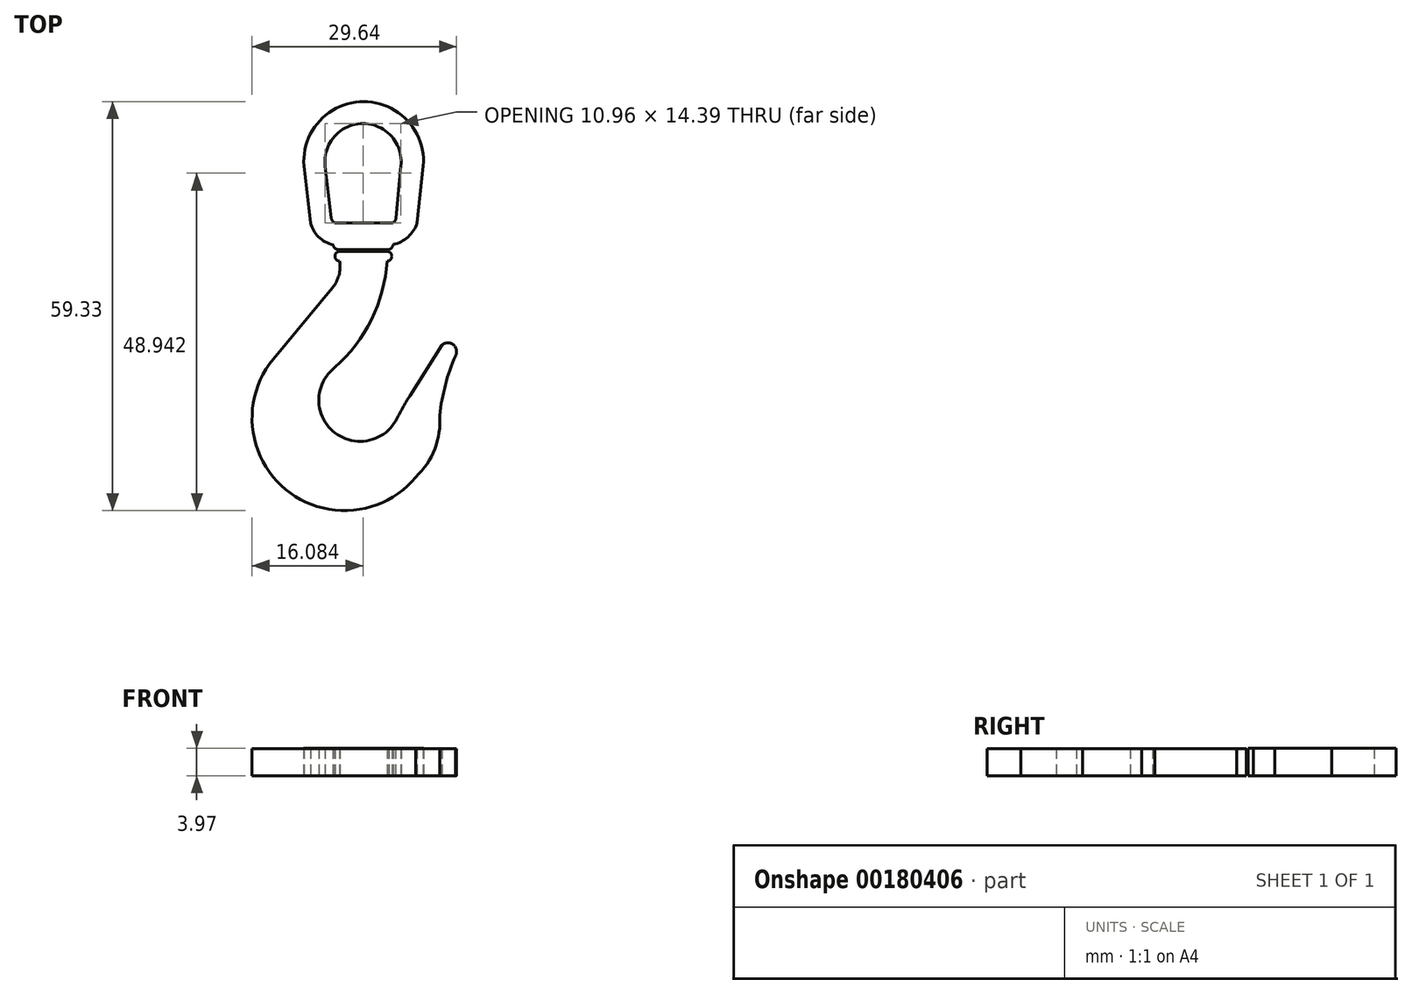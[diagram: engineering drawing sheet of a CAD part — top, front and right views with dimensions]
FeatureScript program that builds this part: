
annotation { "Feature Type Name" : "Feature", "Feature Type Description" : "" }
export const myFeature = defineFeature(function(context is Context, id is Id, definition is map)
    precondition{}
    {
        {
            var Q0;
            Q0=qCreatedBy(makeId("Top.planeOp"),FACE);
            var sketch = newSketch(context, id + "F0", { "sketchPlane" : qUnion([Q0])});
            skLineSegment(sketch, "E0", {"start": v(3.1, -1.85) * mm, "end": v(-3.77, -1.85) * mm});
            skLineSegment(sketch, "E1", {"start": v(-3.77, -3.24) * mm, "end": v(3.1, -3.24) * mm});
            skLineSegment(sketch, "E2", {"start": v(-13.4, -17.47) * mm, "end": v(-4.84, -7.12) * mm});
            skArc(sketch, "E3", {"start": v(-4.84, -7.12) * mm, "mid": v(-3.89, -5.3) * mm, "end": v(-3.77, -3.24) * mm});
            skArc(sketch, "E4", {"start": v(-3.77, -1.85) * mm, "mid": v(-4.46, -2.54) * mm, "end": v(-3.77, -3.24) * mm});
            skArc(sketch, "E5", {"start": v(3.1, -3.24) * mm, "mid": v(3.8, -2.54) * mm, "end": v(3.1, -1.85) * mm});
            skArc(sketch, "E6", {"start": v(-13.4, -17.47) * mm, "mid": v(-11.61, -36.35) * mm, "end": v(7.27, -34.56) * mm});
            skLineSegment(sketch, "E7", {"start": v(6.41, -22.75) * mm, "end": v(11.05, -15.42) * mm});
            skArc(sketch, "E8", {"start": v(-4.5, -18.68) * mm, "mid": v(0.83, -11.71) * mm, "end": v(3.1, -3.24) * mm});
            skArc(sketch, "E9", {"start": v(-4.5, -18.68) * mm, "mid": v(-4.76, -27.9) * mm, "end": v(4.34, -26.44) * mm});
            skArc(sketch, "E10", {"start": v(6.41, -22.75) * mm, "mid": v(5.33, -24.57) * mm, "end": v(4.34, -26.44) * mm});
            skArc(sketch, "E11", {"start": v(13, -17) * mm, "mid": v(12.7, -15.37) * mm, "end": v(11.05, -15.42) * mm});
            skArc(sketch, "E12", {"start": v(7.27, -34.56) * mm, "mid": v(10.01, -30.48) * mm, "end": v(10.73, -25.6) * mm});
            skArc(sketch, "E13", {"start": v(13, -17) * mm, "mid": v(11.55, -21.22) * mm, "end": v(10.73, -25.6) * mm});
            skLineSegment(sketch, "E14", {"start": v(2.13, -1.85) * mm, "end": v(2.13, 2.44) * mm});
            skLineSegment(sketch, "E15", {"start": v(2.13, 2.44) * mm, "end": v(3.1, 2.44) * mm});
            skLineSegment(sketch, "E16", {"start": v(3.1, 2.44) * mm, "end": v(3.1, 5.66) * mm});
            skLineSegment(sketch, "E17", {"start": v(3.1, 5.66) * mm, "end": v(-3.65, 5.66) * mm});
            skLineSegment(sketch, "E18", {"start": v(-3.65, 5.66) * mm, "end": v(-3.65, 2.44) * mm});
            skLineSegment(sketch, "E19", {"start": v(-3.65, 2.44) * mm, "end": v(-2.76, 2.44) * mm});
            skLineSegment(sketch, "E20", {"start": v(-2.76, 2.44) * mm, "end": v(-2.76, -1.85) * mm});
            skSolve(sketch);
        }
        {
            var Q0;
            Q0=qCreatedBy(makeId("Top.planeOp"),FACE);
            var sketch = newSketch(context, id + "F1", { "sketchPlane" : qUnion([Q0])});
            skLineSegment(sketch, "E21", {"start": v(-4.5, 2.32) * mm, "end": v(3.93, 2.32) * mm});
            skLineSegment(sketch, "E22", {"start": v(5.1, 10.55) * mm, "end": v(4.4, 3) * mm});
            skLineSegment(sketch, "E23", {"start": v(-5.86, 10.55) * mm, "end": v(-4.99, 3) * mm});
            skArc(sketch, "E24", {"start": v(-4.99, 3) * mm, "mid": v(-4.83, 2.6) * mm, "end": v(-4.5, 2.32) * mm});
            skArc(sketch, "E25", {"start": v(3.93, 2.32) * mm, "mid": v(4.25, 2.6) * mm, "end": v(4.4, 3) * mm});
            skArc(sketch, "E26", {"start": v(5.1, 10.55) * mm, "mid": v(-0.39, 16.7) * mm, "end": v(-5.86, 10.55) * mm});
            skLineSegment(sketch, "E27", {"start": v(-8.02, 2.32) * mm, "end": v(-8.95, 10.55) * mm});
            skLineSegment(sketch, "E28", {"start": v(8.36, 10.55) * mm, "end": v(7.47, 2.32) * mm});
            skArc(sketch, "E29", {"start": v(8.36, 10.55) * mm, "mid": v(-0.3, 19.9) * mm, "end": v(-8.95, 10.55) * mm});
            skArc(sketch, "E30", {"start": v(4, -0.84) * mm, "mid": v(6.15, 0.28) * mm, "end": v(7.47, 2.32) * mm});
            skArc(sketch, "E31", {"start": v(-8.02, 2.32) * mm, "mid": v(-6.82, 0.25) * mm, "end": v(-4.73, -0.88) * mm});
            skLineSegment(sketch, "E32", {"start": v(-3.93, -1.57) * mm, "end": v(3.35, -1.57) * mm});
            skArc(sketch, "E33", {"start": v(-4.73, -0.88) * mm, "mid": v(-4.46, -1.37) * mm, "end": v(-3.93, -1.57) * mm});
            skArc(sketch, "E34", {"start": v(3.35, -1.57) * mm, "mid": v(3.78, -1.3) * mm, "end": v(4, -0.84) * mm});
            skSolve(sketch);
        }
        {
            var Q0;
            Q0=makeQuery(id+"F1.imprint","IMPRINT",FACE,{"disambiguationData":[TD([[makeQuery(id+"F1.imprint","IMPRINT",EDGE,{"derivedFrom":sQuery(id+"F1.wireOp",EDGE,"E21")}),-1.0]])]});
            extrude(context, id + "F2", {"entities" : qUnion([Q0]), "depth" : 3.97 * mm});
        }
        {
            var Q0;
            Q0=makeQuery(id+"F0.imprint","IMPRINT",FACE,{"disambiguationData":[TD([[makeQuery(id+"F0.imprint","IMPRINT",EDGE,{"derivedFrom":sQuery(id+"F0.wireOp",EDGE,"E1")}),-1.0]])]});
            var Q1;
            Q1=makeQuery(id+"F0.imprint","IMPRINT",FACE,{"disambiguationData":[TD([[makeQuery(id+"F0.imprint","IMPRINT",EDGE,{"derivedFrom":sQuery(id+"F0.wireOp",EDGE,"E1")}),1.0]])]});
            extrude(context, id + "F3", {"entities" : qUnion([Q0, Q1]), "depth" : 3.97 * mm, "offsetDistance" : 25.4 * mm});
        }
    });
